# Revit family: Locker_Benches-Salsbury_Industries-Designer_Wood_77780D_Series
name_source: partatom
category: Specialty Equipment
revit_build: Autodesk Revit 2016 (Build: 20150714_1515(x64)
units: mm (PartAtom-declared; Revit-internal decimal feet)

## family parameters
Always vertical = Yes
Cut with Voids When Loaded = No
OmniClass Number = 23.40.00.00
OmniClass Title = Equipment and Furnishings
Part Type = Normal
Room Calculation Point = No
Round Connector Dimension = Use Diameter
Shared = No
Work Plane-Based = No

## types (6) — shared parameters
Assembly Code = C1030310
Depth = 9.75 "
Height = 18 "
Manufacturer = Salsbury Industries
MasterFormat Number = 10 51 53
MasterFormat Title = Locker Room Benches
OmniClass 23 Number = 23.40.00.00
OmniClass 23 Title = Equipment and Furnishings
Pedestal Material = Aluminum - Salsbury Finish - Black Satin
Primary Material = Wood Laminate - Salsbury Finish - Maple with Industrial Grade Particleboard Underlay
Secondary Material = Melamine - Salsbury Finish - White
Trim Material = Rubber Trim - Salsbury Finish - Black
Type Comments = Designer Wood Locker Bench
URL = www.lockers.com
Version = 1.0 (11/16/18)

## per-type parameters (varying)
| type | Description | Pedestal Offset | Width |
| 77786D | 72 Inches Wide | 6 " | 72.375 " |
| 77787D | 84 Inches Wide | 12 " | 84.375 " |
| 77788D | 96 Inches Wide | 12 " | 96.375 " |
| 77785D | 60 Inches Wide | 6 " | 60.375 " |
| 77784D | 48 Inches Wide | 6 " | 48.375 " |
| 77783D | 36 Inches Wide | 6 " | 36.375 " |

note: column(s) folded — value = type name in every type: Model

## geometry (parser evidence)
native form markers: Sweep x2
no freeform markers — native parametric forms only
